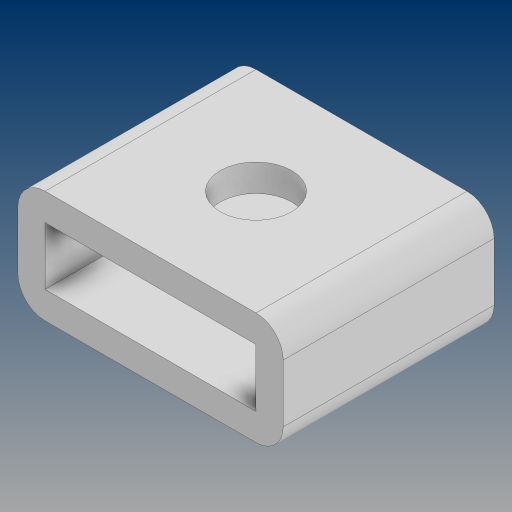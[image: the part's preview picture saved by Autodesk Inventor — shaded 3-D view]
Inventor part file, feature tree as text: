
AUTODESK INVENTOR PART (.ipt)
format: ipt  version: 2023 (Build 270158000, 158)  size: 156,672 bytes
history: native  units: mm
features: extrude x4, sketch x3, plane x1, fillet x1
ambient origin geometry x8: Origin, YZ Plane, XZ Plane, XY Plane, X Axis, Y Axis, Z Axis, Center Point
bodies: Solid1 (feature_tree)
feature tree (9):
  sketch  "Sketch1"  dims[d0=15.5mm d1=15.5mm]
  extrude  "Extrusion1"  Depth=15.5mm
  extrude  "Extrusion2"  Depth=2.0mm
  plane  "Work Plane1"
  extrude  "Extrusion3"  Depth=2.0mm TaperAngle=0.0deg
  extrude  "Extrusion4"  Depth=8.25mm TaperAngle=0.0deg
  fillet  "Fillet2"  Radius=5.25mm
  sketch  "Sketch2"  dims[d2=2.0mm d3=2.0mm]
  sketch  "Sketch3"  dims[d4=5.25mm d5=2.0mm d6=0.0mm d7=8.25mm d8=0.0mm d9=5.25mm d10=2.0mm d11=0.0mm d13=15.0mm d14=0.5mm d15=0.0mm d16=2.0mm]
